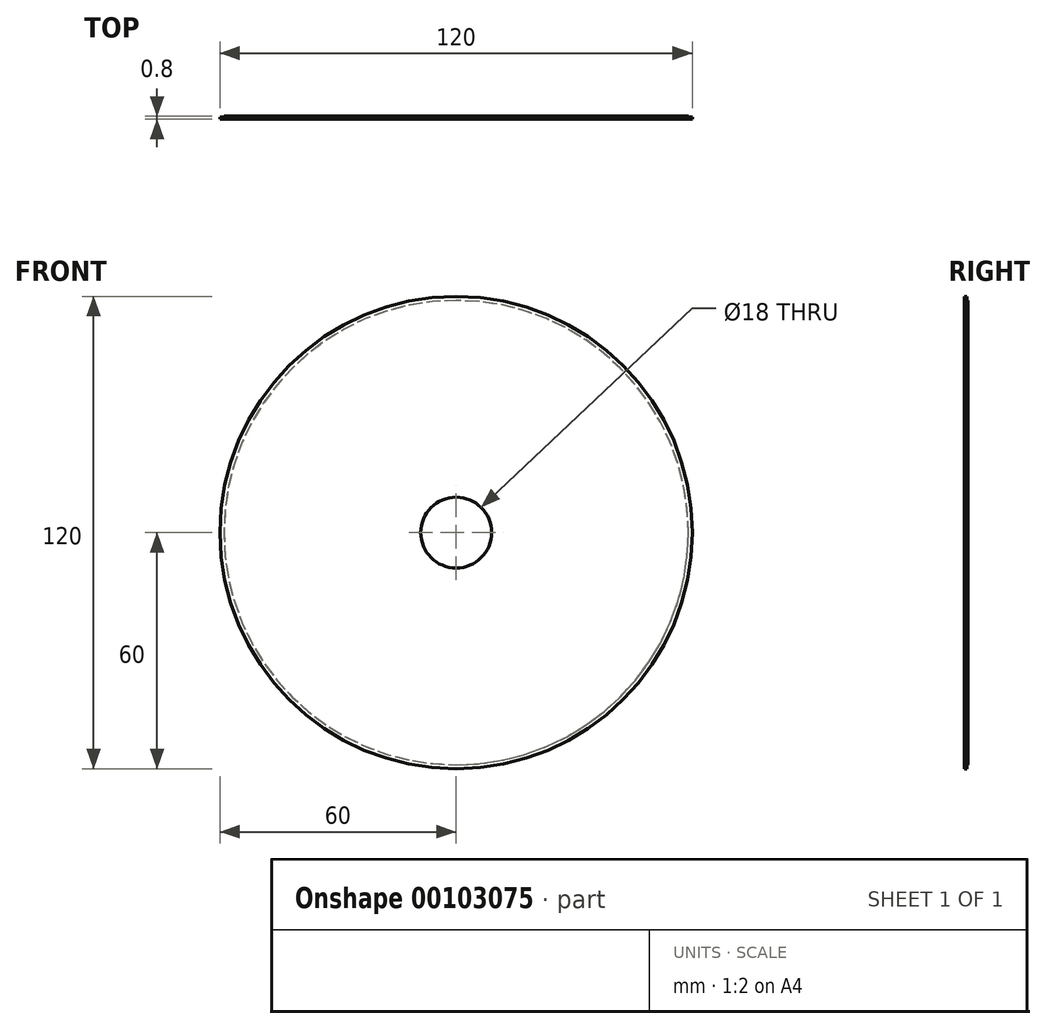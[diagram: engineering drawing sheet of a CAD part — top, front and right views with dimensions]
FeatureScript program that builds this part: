
annotation { "Feature Type Name" : "Feature", "Feature Type Description" : "" }
export const myFeature = defineFeature(function(context is Context, id is Id, definition is map)
    precondition{}
    {
        {
            var Q0;
            Q0=qCreatedBy(makeId("Front.planeOp"),FACE);
            var sketch = newSketch(context, id + "F0", { "sketchPlane" : qUnion([Q0])});
            skCircle(sketch, "E0", {"center": v(0, 0) * mm, "radius": 60 * mm});
            skCircle(sketch, "E1", {"center": v(0, 0) * mm, "radius": 9 * mm});
            skSolve(sketch);
        }
        {
            var Q0;
            Q0=makeQuery(id+"F0.imprint","IMPRINT",FACE,{"disambiguationData":[TD([[makeQuery(id+"F0.imprint","IMPRINT",EDGE,{"derivedFrom":sQuery(id+"F0.wireOp",EDGE,"E0")}),1.0]])]});
            extrude(context, id + "F1", {"entities" : qUnion([Q0]), "endBound" : BoundingType.SYMMETRIC, "depth" : 0.3 * mm});
        }
        {
            var Q0;
            Q0=makeQuery(id+"F1.opExtrude","CAP_FACE",FACE,{"disambiguationData":[OSD([sQuery(id+"F0.wireOp",EDGE,"E0"),sQuery(id+"F0.wireOp",EDGE,"E1")])],"isStart":true});
            var sketch = newSketch(context, id + "F2", { "sketchPlane" : qUnion([Q0])});
            skCircle(sketch, "E2", {"center": v(0, 0) * mm, "radius": 59 * mm});
            skSolve(sketch);
        }
        {
            var Q0;
            Q0 = qSketchRegion(id + "F2", true);
            var Q1;
            Q1=makeQuery(id+"F1.opExtrude","CAP_FACE",FACE,{"disambiguationData":[OSD([sQuery(id+"F0.wireOp",EDGE,"E0"),sQuery(id+"F0.wireOp",EDGE,"E1")])],"isStart":false});
            extrude(context, id + "F3", {"entities" : qUnion([Q0, Q1]), "operationType" : NewBodyOperationType.ADD, "endBound" : BoundingType.SYMMETRIC, "depth" : 0.5 * mm});
        }
        {
            var Q0;
            Q0=makeQuery(id+"F3.opExtrude","CAP_FACE",FACE,{"disambiguationData":[OSD([sQuery(id+"F2.wireOp",EDGE,"E2")])],"isStart":true});
            extrude(context, id + "F4", {"entities" : qUnion([Q0]), "operationType" : NewBodyOperationType.REMOVE, "endBound" : BoundingType.THROUGH_ALL, "oppositeDirection" : true, "depth" : 25.4 * mm});
        }
    });
